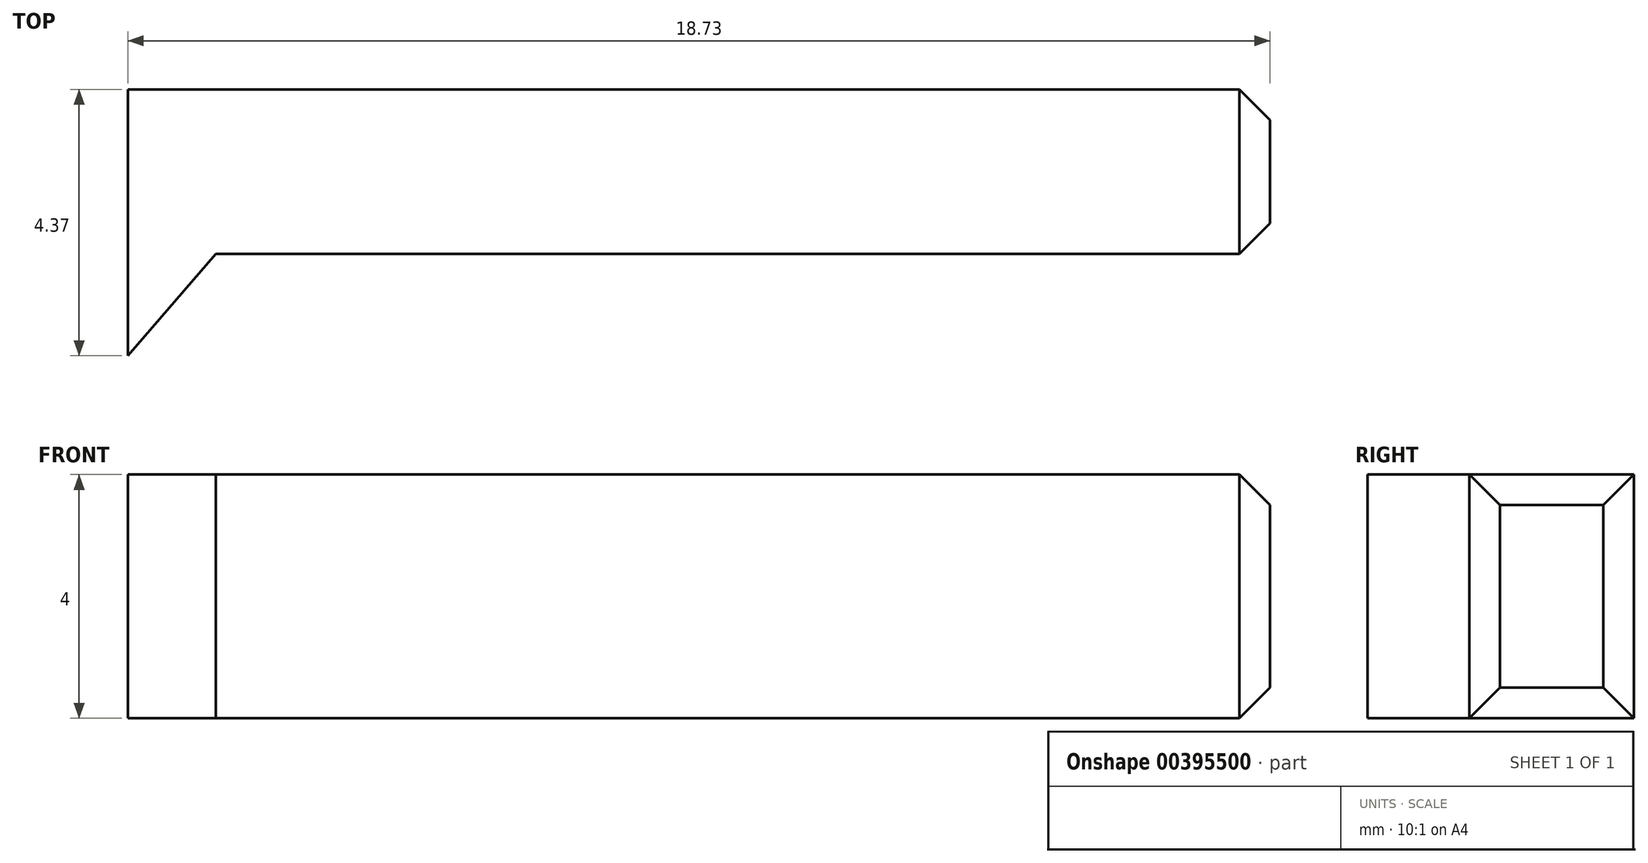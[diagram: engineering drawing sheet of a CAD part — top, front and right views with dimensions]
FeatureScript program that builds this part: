
annotation { "Feature Type Name" : "Feature", "Feature Type Description" : "" }
export const myFeature = defineFeature(function(context is Context, id is Id, definition is map)
    precondition{}
    {
        {
            var Q0;
            Q0=qCreatedBy(makeId("Top.planeOp"),FACE);
            var sketch = newSketch(context, id + "F0", { "sketchPlane" : qUnion([Q0])});
            skLineSegment(sketch, "E0", {"start": v(18.73, 0) * mm, "end": v(0, 0) * mm});
            skLineSegment(sketch, "E1", {"start": v(0, 0) * mm, "end": v(0, -4.37) * mm});
            skPoint(sketch, "E2.orphan", {"position": v(0.23, -2.75) * mm});
            skPoint(sketch, "E3.visualSharp", {"position": v(19.23, 0) * mm});
            skPoint(sketch, "E4.visualSharp", {"position": v(19.23, -2.75) * mm});
            skLineSegment(sketch, "E5", {"start": v(18.73, 0) * mm, "end": v(18.73, -2.7) * mm});
            skLineSegment(sketch, "E6", {"start": v(18.73, -2.7) * mm, "end": v(1.44, -2.7) * mm});
            skLineSegment(sketch, "E7", {"start": v(0, -4.37) * mm, "end": v(1.44, -2.7) * mm});
            skSolve(sketch);
        }
        {
            var Q0;
            Q0=makeQuery(id+"F0.imprint","IMPRINT",FACE,{"disambiguationData":[TD([[makeQuery(id+"F0.imprint","IMPRINT",EDGE,{"derivedFrom":sQuery(id+"F0.wireOp",EDGE,"E0")}),1.0]])]});
            extrude(context, id + "F1", {"entities" : qUnion([Q0]), "oppositeDirection" : true, "depth" : 4 * mm});
        }
        {
            var Q0;
            Q0=makeQuery(id+"F1.opExtrude","SWEPT_EDGE",EDGE,{"disambiguationData":[OSD([sQuery(id+"F0.wireOp",EDGE,"E5"),sQuery(id+"F0.wireOp",EDGE,"E6")])]});
            var Q1;
            Q1=makeQuery(id+"F1.opExtrude","CAP_EDGE",EDGE,{"disambiguationData":[OSD([sQuery(id+"F0.wireOp",EDGE,"E5")])],"isStart":true});
            var Q2;
            Q2=makeQuery(id+"F1.opExtrude","SWEPT_EDGE",EDGE,{"disambiguationData":[OSD([sQuery(id+"F0.wireOp",EDGE,"E0"),sQuery(id+"F0.wireOp",EDGE,"E5")])]});
            var Q3;
            Q3=makeQuery(id+"F1.opExtrude","CAP_EDGE",EDGE,{"disambiguationData":[OSD([sQuery(id+"F0.wireOp",EDGE,"E5")])],"isStart":false});
            chamfer(context, id + "F2", {"entities" : qUnion([Q0, Q1, Q2, Q3]), "width" : .5 * mm, "tangentPropagation" : true});
        }
    });
